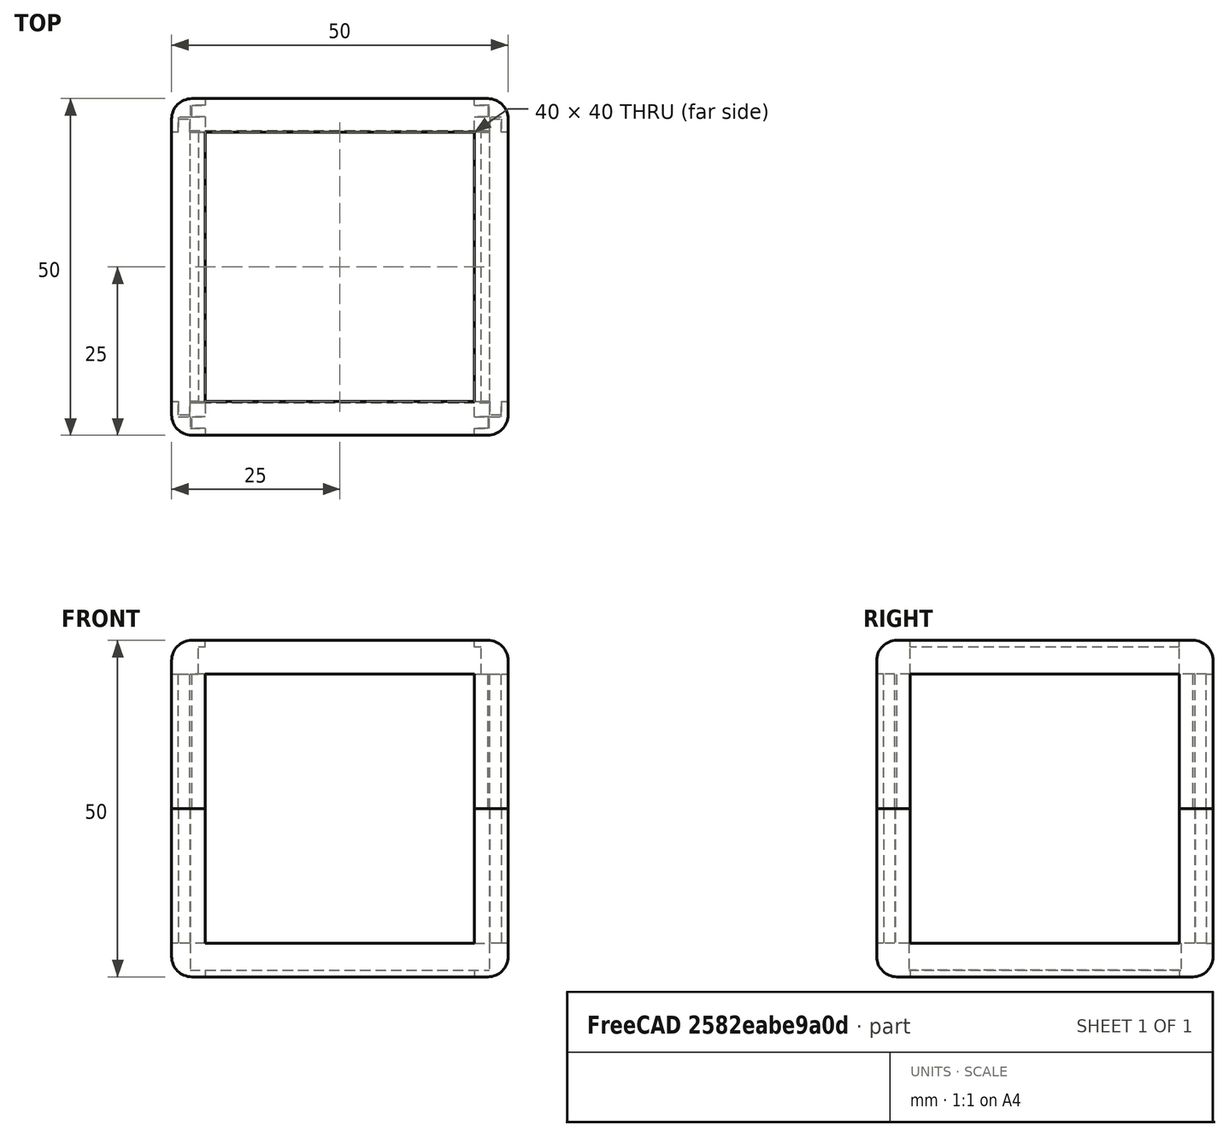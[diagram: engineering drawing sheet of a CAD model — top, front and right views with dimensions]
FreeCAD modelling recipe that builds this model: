
FCSTD DOCUMENT  (FreeCAD 0.18.4R)
Label: frame
License: All rights reserved
LicenseURL: http://en.wikipedia.org/wiki/All_rights_reserved
objects: Sketcher::SketchObject×8, PartDesign::Pocket×6, PartDesign::Pad×2, PartDesign::Fillet×2, PartDesign::Body×2, Mesh::Feature×1
note: 28 computed .brp shape members not serialized (recipe doc carries the construction recipe); baked Part::Feature solids carry a one-line shape summary decoded from their .brp

FEATURE [Sketcher::SketchObject] Sketch
  MapMode = 5
  Support = -> [XY_Plane]
  sketch-geometry (4):
    g0: LineSegment StartX=-25 StartY=25 StartZ=0 EndX=25 EndY=25 EndZ=0
    g1: LineSegment StartX=25 StartY=25 StartZ=0 EndX=25 EndY=-25 EndZ=0
    g2: LineSegment StartX=25 StartY=-25 StartZ=0 EndX=-25 EndY=-25 EndZ=0
    g3: LineSegment StartX=-25 StartY=-25 StartZ=0 EndX=-25 EndY=25 EndZ=0
  constraints (10):
    c: Coincident(g0,g1)
    c: Coincident(g1,g2)
    c: Coincident(g2,g3)
    c: Coincident(g3,g0)
    c: Horizontal(g0)
    c: Vertical(g3)
    c: DistanceX(g0,g0) = 50
    c: DistanceY(g1,g1) = 50
    c: Symmetric(g2,g1,g-2)
    c: Symmetric(g0,g1,g-1)
FEATURE [PartDesign::Pad] Pad
  Length = 25
  Length2 = 100
  Profile = -> Sketch
  Type = 0
FEATURE [PartDesign::Fillet] Fillet
  Base = -> Pad [Edge9,Edge11,Edge3,Edge6,Edge8,Edge2,Edge1,Edge5]
  BaseFeature = -> Pad
  Radius = 3
FEATURE [Sketcher::SketchObject] Sketch007
  MapMode = 5
  Placement = pos=(0,0,25) rot=(0,0,1;0rad)
  Support = -> [Fillet]
  sketch-geometry (44):
    g0: LineSegment StartX=-20 StartY=25 StartZ=0 EndX=-20 EndY=24 EndZ=0
    g1: LineSegment StartX=-20 StartY=24 StartZ=0 EndX=-22.25 EndY=24 EndZ=0
    g2: LineSegment StartX=-22.25 StartY=24 StartZ=0 EndX=-22.25 EndY=22.3 EndZ=0
    g3: LineSegment StartX=-22.25 StartY=22.3 StartZ=0 EndX=-20 EndY=22.3 EndZ=0
    g4: LineSegment StartX=-20 StartY=22.3 StartZ=0 EndX=-20 EndY=20 EndZ=0
    g5: LineSegment StartX=-20 StartY=20 StartZ=0 EndX=-22.3 EndY=20 EndZ=0
    g6: LineSegment StartX=-22.3 StartY=20 StartZ=0 EndX=-22.3 EndY=22.25 EndZ=0
    g7: LineSegment StartX=-22.3 StartY=22.25 StartZ=0 EndX=-24 EndY=22.25 EndZ=0
    g8: LineSegment StartX=-24 StartY=22.25 StartZ=0 EndX=-24 EndY=20 EndZ=0
    g9: LineSegment StartX=-24 StartY=20 StartZ=0 EndX=-25 EndY=20 EndZ=0
    g10: LineSegment StartX=-25 StartY=20 StartZ=0 EndX=-25 EndY=-20 EndZ=0
    g11: LineSegment StartX=-25 StartY=-20 StartZ=0 EndX=-24 EndY=-20 EndZ=0
    g12: LineSegment StartX=-24 StartY=-20 StartZ=0 EndX=-24 EndY=-22.25 EndZ=0
    g13: LineSegment StartX=-24 StartY=-22.25 StartZ=0 EndX=-22.3 EndY=-22.25 EndZ=0
    g14: LineSegment StartX=-22.3 StartY=-22.25 StartZ=0 EndX=-22.3 EndY=-20 EndZ=0
    g15: LineSegment StartX=-22.3 StartY=-20 StartZ=0 EndX=-20 EndY=-20 EndZ=0
    g16: LineSegment StartX=-20 StartY=-20 StartZ=0 EndX=-20 EndY=-22.3 EndZ=0
    g17: LineSegment StartX=-20 StartY=-22.3 StartZ=0 EndX=-22.25 EndY=-22.3 EndZ=0
    g18: LineSegment StartX=-22.25 StartY=-22.3 StartZ=0 EndX=-22.25 EndY=-24 EndZ=0
    g19: LineSegment StartX=-22.25 StartY=-24 StartZ=0 EndX=-20 EndY=-24 EndZ=0
    g20: LineSegment StartX=-20 StartY=-24 StartZ=0 EndX=-20 EndY=-25 EndZ=0
    g21: LineSegment StartX=-20 StartY=-25 StartZ=0 EndX=20 EndY=-25 EndZ=0
    g22: LineSegment StartX=20 StartY=-25 StartZ=0 EndX=20 EndY=-24 EndZ=0
    g23: LineSegment StartX=20 StartY=-24 StartZ=0 EndX=22.25 EndY=-24 EndZ=0
    g24: LineSegment StartX=22.25 StartY=-24 StartZ=0 EndX=22.25 EndY=-22.3 EndZ=0
    g25: LineSegment StartX=22.25 StartY=-22.3 StartZ=0 EndX=20 EndY=-22.3 EndZ=0
    g26: LineSegment StartX=20 StartY=-22.3 StartZ=0 EndX=20 EndY=-20 EndZ=0
    g27: LineSegment StartX=20 StartY=-20 StartZ=0 EndX=22.3 EndY=-20 EndZ=0
    g28: LineSegment StartX=22.3 StartY=-20 StartZ=0 EndX=22.3 EndY=-22.25 EndZ=0
    g29: LineSegment StartX=22.3 StartY=-22.25 StartZ=0 EndX=24 EndY=-22.25 EndZ=0
    g30: LineSegment StartX=24 StartY=-22.25 StartZ=0 EndX=24 EndY=-20 EndZ=0
    g31: LineSegment StartX=24 StartY=-20 StartZ=0 EndX=25 EndY=-20 EndZ=0
    g32: LineSegment StartX=25 StartY=-20 StartZ=0 EndX=25 EndY=20 EndZ=0
    g33: LineSegment StartX=25 StartY=20 StartZ=0 EndX=24 EndY=20 EndZ=0
    g34: LineSegment StartX=24 StartY=20 StartZ=0 EndX=24 EndY=22.25 EndZ=0
    g35: LineSegment StartX=24 StartY=22.25 StartZ=0 EndX=22.3 EndY=22.25 EndZ=0
    g36: LineSegment StartX=22.3 StartY=22.25 StartZ=0 EndX=22.3 EndY=20 EndZ=0
    g37: LineSegment StartX=22.3 StartY=20 StartZ=0 EndX=20 EndY=20 EndZ=0
    g38: LineSegment StartX=20 StartY=20 StartZ=0 EndX=20 EndY=22.3 EndZ=0
    g39: LineSegment StartX=20 StartY=22.3 StartZ=0 EndX=22.25 EndY=22.3 EndZ=0
    g40: LineSegment StartX=22.25 StartY=22.3 StartZ=0 EndX=22.25 EndY=24 EndZ=0
    g41: LineSegment StartX=22.25 StartY=24 StartZ=0 EndX=20 EndY=24 EndZ=0
    g42: LineSegment StartX=20 StartY=24 StartZ=0 EndX=20 EndY=25 EndZ=0
    g43: LineSegment StartX=20 StartY=25 StartZ=0 EndX=-20 EndY=25 EndZ=0
  constraints (130):
    c: Coincident(g0,g1)
    c: Coincident(g1,g2)
    c: Coincident(g2,g3)
    c: Coincident(g3,g4)
    c: Coincident(g4,g5)
    c: Horizontal(g5)
    c: Coincident(g5,g6)
    c: Vertical(g6)
    c: Coincident(g6,g7)
    c: Horizontal(g7)
    c: Coincident(g7,g8)
    c: Vertical(g8)
    c: Coincident(g8,g9)
    c: Coincident(g9,g10)
    c: Vertical(g10)
    c: Coincident(g10,g11)
    c: Coincident(g11,g12)
    c: Coincident(g12,g13)
    c: Coincident(g13,g14)
    c: Vertical(g14)
    c: Coincident(g14,g15)
    c: Horizontal(g15)
    c: Coincident(g15,g16)
    c: Coincident(g16,g17)
    c: Horizontal(g17)
    c: Coincident(g17,g18)
    c: Coincident(g18,g19)
    c: Coincident(g19,g20)
    c: Coincident(g20,g21)
    c: Horizontal(g21)
    c: Coincident(g21,g22)
    c: Coincident(g22,g23)
    c: Horizontal(g23)
    c: Coincident(g23,g24)
    c: Coincident(g24,g25)
    c: Horizontal(g25)
    c: Coincident(g25,g26)
    c: Vertical(g26)
    c: Coincident(g26,g27)
    c: Coincident(g27,g28)
    c: Coincident(g28,g29)
    c: Coincident(g29,g30)
    c: Vertical(g30)
    c: Coincident(g30,g31)
    c: Horizontal(g31)
    c: Coincident(g31,g32)
    c: Vertical(g32)
    c: Coincident(g32,g33)
    c: Coincident(g33,g34)
    c: Vertical(g34)
    c: Coincident(g34,g35)
    c: Coincident(g35,g36)
    c: Coincident(g36,g37)
    c: Coincident(g37,g38)
    c: Coincident(g38,g39)
    c: Coincident(g39,g40)
    c: Coincident(g40,g41)
    c: Coincident(g41,g42)
    c: Vertical(g42)
    c: Coincident(g42,g43)
    c: Coincident(g43,g0)
    c: Equal(g43,g21)
    c: Horizontal(g43)
    c: Equal(g10,g32)
    c: Horizontal(g13)
    c: Horizontal(g11)
    c: Vertical(g16)
    c: Vertical(g12)
    c: Vertical(g18)
    c: Vertical(g20)
    c: Horizontal(g19)
    c: Vertical(g22)
    c: Vertical(g24)
    c: Vertical(g28)
    c: Vertical(g36)
    c: Vertical(g38)
    c: Vertical(g2)
    c: Vertical(g0)
    c: Horizontal(g1)
    c: Horizontal(g3)
    c: Horizontal(g9)
    c: Horizontal(g27)
    c: Horizontal(g33)
    c: Horizontal(g35)
    c: Horizontal(g37)
    c: Horizontal(g39)
    c: Equal(g2,g40)
    c: Equal(g40,g18)
    c: Equal(g18,g24)
    c: Equal(g13,g29)
    c: Equal(g29,g35)
    c: Equal(g35,g7)
    c: Equal(g33,g9)
    c: Equal(g9,g11)
    c: Equal(g11,g31)
    c: Equal(g22,g20)
    c: Equal(g20,g0)
    c: Equal(g0,g42)
    c: Equal(g4,g38)
    c: Equal(g38,g26)
    c: Equal(g26,g16)
    c: Equal(g15,g27)
    c: Equal(g27,g37)
    c: Equal(g37,g5)
    c: Equal(g8,g6)
    c: Equal(g6,g36)
    c: Equal(g36,g34)
    c: Equal(g34,g12)
    c: Equal(g12,g14)
    c: Equal(g14,g28)
    c: Equal(g28,g30)
    c: Equal(g25,g23)
    c: Equal(g23,g17)
    c: Equal(g17,g19)
    c: Equal(g19,g1)
    c: Equal(g1,g3)
    c: Equal(g3,g41)
    c: Equal(g41,g39)
    c: DistanceX(g43,g43) = 40
    c: DistanceY(g32,g32) = 40
    c: DistanceY(g12,g7) = 44.5
    c: DistanceX(g1,g40) = 44.5
    c: DistanceY(g20,g0) = 50
    c: DistanceX(g10,g31) = 50
    c: Symmetric(g21,g42,g-1)
    c: Symmetric(g9,g32,g-2)
    c: DistanceX(g13,g13) = 1.7
    c: DistanceX(g11,g11) = 1
    c: DistanceY(g20,g20) = 1
    c: DistanceY(g18,g18) = 1.7
FEATURE [PartDesign::Pocket] Pocket
  BaseFeature = -> Fillet
  Length = 20
  Length2 = 100
  Profile = -> Sketch007
  Type = 0
FEATURE [Mesh::Feature] screen
  Placement = pos=(-18,10,5.5) rot=(-1,0,0;3.14159rad)
FEATURE [Sketcher::SketchObject] Sketch008
  MapMode = 5
  Placement = pos=(0,0,5) rot=(0,0,1;0rad)
  Support = -> [Pocket]
  sketch-geometry (4):
    g0: LineSegment StartX=-22.25 StartY=20.25 StartZ=0 EndX=22.25 EndY=20.25 EndZ=0
    g1: LineSegment StartX=22.25 StartY=20.25 StartZ=0 EndX=22.25 EndY=-20.25 EndZ=0
    g2: LineSegment StartX=22.25 StartY=-20.25 StartZ=0 EndX=-22.25 EndY=-20.25 EndZ=0
    g3: LineSegment StartX=-22.25 StartY=-20.25 StartZ=0 EndX=-22.25 EndY=20.25 EndZ=0
  constraints (10):
    c: Coincident(g0,g1)
    c: Coincident(g1,g2)
    c: Coincident(g2,g3)
    c: Coincident(g3,g0)
    c: Horizontal(g0)
    c: Vertical(g3)
    c: DistanceX(g0,g0) = 44.5
    c: DistanceY(g1,g1) = 40.5
    c: Symmetric(g2,g1,g-2)
    c: Symmetric(g0,g1,g-1)
FEATURE [PartDesign::Pocket] Pocket001
  BaseFeature = -> Pocket
  Length = 4
  Length2 = 100
  Profile = -> Sketch008
  Type = 0
FEATURE [Sketcher::SketchObject] Sketch009
  MapMode = 5
  Placement = pos=(0,0,1) rot=(0,0,1;0rad)
  Support = -> [Pocket001]
  sketch-geometry (4):
    g0: LineSegment StartX=-20 StartY=20 StartZ=0 EndX=20 EndY=20 EndZ=0
    g1: LineSegment StartX=20 StartY=20 StartZ=0 EndX=20 EndY=-20 EndZ=0
    g2: LineSegment StartX=20 StartY=-20 StartZ=0 EndX=-20 EndY=-20 EndZ=0
    g3: LineSegment StartX=-20 StartY=-20 StartZ=0 EndX=-20 EndY=20 EndZ=0
  constraints (10):
    c: Coincident(g0,g1)
    c: Coincident(g1,g2)
    c: Coincident(g2,g3)
    c: Coincident(g3,g0)
    c: Horizontal(g0)
    c: Vertical(g3)
    c: DistanceY(g1,g1) = 40
    c: DistanceX(g2,g2) = 40
    c: Symmetric(g2,g1,g-2)
    c: Symmetric(g0,g1,g-1)
FEATURE [PartDesign::Pocket] Pocket002
  BaseFeature = -> Pocket001
  Length = 1
  Length2 = 100
  Profile = -> Sketch009
  Type = 0
FEATURE [PartDesign::Body] Body  label="Bottom"
  Group = -> [Sketch,Pad,Fillet,Sketch007,Pocket,Sketch008,Pocket001,Sketch009,Pocket002]
  Origin = -> Origin
  Tip = -> Pocket002
FEATURE [Sketcher::SketchObject] Sketch011
  MapMode = 5
  Support = -> [XY_Plane001]
  sketch-geometry (4):
    g0: LineSegment StartX=-25 StartY=25 StartZ=0 EndX=25 EndY=25 EndZ=0
    g1: LineSegment StartX=25 StartY=25 StartZ=0 EndX=25 EndY=-25 EndZ=0
    g2: LineSegment StartX=25 StartY=-25 StartZ=0 EndX=-25 EndY=-25 EndZ=0
    g3: LineSegment StartX=-25 StartY=-25 StartZ=0 EndX=-25 EndY=25 EndZ=0
  constraints (10):
    c: Coincident(g0,g1)
    c: Coincident(g1,g2)
    c: Coincident(g2,g3)
    c: Coincident(g3,g0)
    c: Horizontal(g0)
    c: Vertical(g3)
    c: DistanceX(g0,g0) = 50
    c: DistanceY(g1,g1) = 50
    c: Symmetric(g2,g1,g-2)
    c: Symmetric(g0,g1,g-1)
FEATURE [PartDesign::Pad] Pad001
  Length = 25
  Length2 = 100
  Profile = -> Sketch011
  Type = 0
FEATURE [PartDesign::Fillet] Fillet001
  Base = -> Pad001 [Edge9,Edge11,Edge3,Edge6,Edge8,Edge2,Edge1,Edge5]
  BaseFeature = -> Pad001
  Radius = 3
FEATURE [Sketcher::SketchObject] Sketch012
  MapMode = 5
  Placement = pos=(0,0,25) rot=(0,0,1;0rad)
  Support = -> [Fillet001]
  sketch-geometry (44):
    g0: LineSegment StartX=-20 StartY=25 StartZ=0 EndX=-20 EndY=24 EndZ=0
    g1: LineSegment StartX=-20 StartY=24 StartZ=0 EndX=-22 EndY=24 EndZ=0
    g2: LineSegment StartX=-22 StartY=24 StartZ=0 EndX=-22 EndY=22.3 EndZ=0
    g3: LineSegment StartX=-22 StartY=22.3 StartZ=0 EndX=-20 EndY=22.3 EndZ=0
    g4: LineSegment StartX=-20 StartY=22.3 StartZ=0 EndX=-20 EndY=20 EndZ=0
    g5: LineSegment StartX=-20 StartY=20 StartZ=0 EndX=-22.3 EndY=20 EndZ=0
    g6: LineSegment StartX=-22.3 StartY=20 StartZ=0 EndX=-22.3 EndY=22 EndZ=0
    g7: LineSegment StartX=-22.3 StartY=22 StartZ=0 EndX=-24 EndY=22 EndZ=0
    g8: LineSegment StartX=-24 StartY=22 StartZ=0 EndX=-24 EndY=20 EndZ=0
    g9: LineSegment StartX=-24 StartY=20 StartZ=0 EndX=-25 EndY=20 EndZ=0
    g10: LineSegment StartX=-25 StartY=20 StartZ=0 EndX=-25 EndY=-20 EndZ=0
    g11: LineSegment StartX=-25 StartY=-20 StartZ=0 EndX=-24 EndY=-20 EndZ=0
    g12: LineSegment StartX=-24 StartY=-20 StartZ=0 EndX=-24 EndY=-22 EndZ=0
    g13: LineSegment StartX=-24 StartY=-22 StartZ=0 EndX=-22.3 EndY=-22 EndZ=0
    g14: LineSegment StartX=-22.3 StartY=-22 StartZ=0 EndX=-22.3 EndY=-20 EndZ=0
    g15: LineSegment StartX=-22.3 StartY=-20 StartZ=0 EndX=-20 EndY=-20 EndZ=0
    g16: LineSegment StartX=-20 StartY=-20 StartZ=0 EndX=-20 EndY=-22.3 EndZ=0
    g17: LineSegment StartX=-20 StartY=-22.3 StartZ=0 EndX=-22 EndY=-22.3 EndZ=0
    g18: LineSegment StartX=-22 StartY=-22.3 StartZ=0 EndX=-22 EndY=-24 EndZ=0
    g19: LineSegment StartX=-22 StartY=-24 StartZ=0 EndX=-20 EndY=-24 EndZ=0
    g20: LineSegment StartX=-20 StartY=-24 StartZ=0 EndX=-20 EndY=-25 EndZ=0
    g21: LineSegment StartX=-20 StartY=-25 StartZ=0 EndX=20 EndY=-25 EndZ=0
    g22: LineSegment StartX=20 StartY=-25 StartZ=0 EndX=20 EndY=-24 EndZ=0
    g23: LineSegment StartX=20 StartY=-24 StartZ=0 EndX=22 EndY=-24 EndZ=0
    g24: LineSegment StartX=22 StartY=-24 StartZ=0 EndX=22 EndY=-22.3 EndZ=0
    g25: LineSegment StartX=22 StartY=-22.3 StartZ=0 EndX=20 EndY=-22.3 EndZ=0
    g26: LineSegment StartX=20 StartY=-22.3 StartZ=0 EndX=20 EndY=-20 EndZ=0
    g27: LineSegment StartX=20 StartY=-20 StartZ=0 EndX=22.3 EndY=-20 EndZ=0
    g28: LineSegment StartX=22.3 StartY=-20 StartZ=0 EndX=22.3 EndY=-22 EndZ=0
    g29: LineSegment StartX=22.3 StartY=-22 StartZ=0 EndX=24 EndY=-22 EndZ=0
    g30: LineSegment StartX=24 StartY=-22 StartZ=0 EndX=24 EndY=-20 EndZ=0
    g31: LineSegment StartX=24 StartY=-20 StartZ=0 EndX=25 EndY=-20 EndZ=0
    g32: LineSegment StartX=25 StartY=-20 StartZ=0 EndX=25 EndY=20 EndZ=0
    g33: LineSegment StartX=25 StartY=20 StartZ=0 EndX=24 EndY=20 EndZ=0
    g34: LineSegment StartX=24 StartY=20 StartZ=0 EndX=24 EndY=22 EndZ=0
    g35: LineSegment StartX=24 StartY=22 StartZ=0 EndX=22.3 EndY=22 EndZ=0
    g36: LineSegment StartX=22.3 StartY=22 StartZ=0 EndX=22.3 EndY=20 EndZ=0
    g37: LineSegment StartX=22.3 StartY=20 StartZ=0 EndX=20 EndY=20 EndZ=0
    g38: LineSegment StartX=20 StartY=20 StartZ=0 EndX=20 EndY=22.3 EndZ=0
    g39: LineSegment StartX=20 StartY=22.3 StartZ=0 EndX=22 EndY=22.3 EndZ=0
    g40: LineSegment StartX=22 StartY=22.3 StartZ=0 EndX=22 EndY=24 EndZ=0
    g41: LineSegment StartX=22 StartY=24 StartZ=0 EndX=20 EndY=24 EndZ=0
    g42: LineSegment StartX=20 StartY=24 StartZ=0 EndX=20 EndY=25 EndZ=0
    g43: LineSegment StartX=20 StartY=25 StartZ=0 EndX=-20 EndY=25 EndZ=0
  constraints (130):
    c: Coincident(g0,g1)
    c: Coincident(g1,g2)
    c: Coincident(g2,g3)
    c: Coincident(g3,g4)
    c: Coincident(g4,g5)
    c: Horizontal(g5)
    c: Coincident(g5,g6)
    c: Vertical(g6)
    c: Coincident(g6,g7)
    c: Horizontal(g7)
    c: Coincident(g7,g8)
    c: Vertical(g8)
    c: Coincident(g8,g9)
    c: Coincident(g9,g10)
    c: Vertical(g10)
    c: Coincident(g10,g11)
    c: Coincident(g11,g12)
    c: Coincident(g12,g13)
    c: Coincident(g13,g14)
    c: Vertical(g14)
    c: Coincident(g14,g15)
    c: Horizontal(g15)
    c: Coincident(g15,g16)
    c: Coincident(g16,g17)
    c: Horizontal(g17)
    c: Coincident(g17,g18)
    c: Coincident(g18,g19)
    c: Coincident(g19,g20)
    c: Coincident(g20,g21)
    c: Horizontal(g21)
    c: Coincident(g21,g22)
    c: Coincident(g22,g23)
    c: Horizontal(g23)
    c: Coincident(g23,g24)
    c: Coincident(g24,g25)
    c: Horizontal(g25)
    c: Coincident(g25,g26)
    c: Vertical(g26)
    c: Coincident(g26,g27)
    c: Coincident(g27,g28)
    c: Coincident(g28,g29)
    c: Coincident(g29,g30)
    c: Vertical(g30)
    c: Coincident(g30,g31)
    c: Horizontal(g31)
    c: Coincident(g31,g32)
    c: Vertical(g32)
    c: Coincident(g32,g33)
    c: Coincident(g33,g34)
    c: Vertical(g34)
    c: Coincident(g34,g35)
    c: Coincident(g35,g36)
    c: Coincident(g36,g37)
    c: Coincident(g37,g38)
    c: Coincident(g38,g39)
    c: Coincident(g39,g40)
    c: Coincident(g40,g41)
    c: Coincident(g41,g42)
    c: Vertical(g42)
    c: Coincident(g42,g43)
    c: Coincident(g43,g0)
    c: Equal(g43,g21)
    c: Horizontal(g43)
    c: Equal(g10,g32)
    c: Horizontal(g13)
    c: Horizontal(g11)
    c: Vertical(g16)
    c: Vertical(g12)
    c: Vertical(g18)
    c: Vertical(g20)
    c: Horizontal(g19)
    c: Vertical(g22)
    c: Vertical(g24)
    c: Vertical(g28)
    c: Vertical(g36)
    c: Vertical(g38)
    c: Vertical(g2)
    c: Vertical(g0)
    c: Horizontal(g1)
    c: Horizontal(g3)
    c: Horizontal(g9)
    c: Horizontal(g27)
    c: Horizontal(g33)
    c: Horizontal(g35)
    c: Horizontal(g37)
    c: Horizontal(g39)
    c: Equal(g2,g40)
    c: Equal(g40,g18)
    c: Equal(g18,g24)
    c: Equal(g13,g29)
    c: Equal(g29,g35)
    c: Equal(g35,g7)
    c: Equal(g33,g9)
    c: Equal(g9,g11)
    c: Equal(g11,g31)
    c: Equal(g22,g20)
    c: Equal(g20,g0)
    c: Equal(g0,g42)
    c: Equal(g4,g38)
    c: Equal(g38,g26)
    c: Equal(g26,g16)
    c: Equal(g15,g27)
    c: Equal(g27,g37)
    c: Equal(g37,g5)
    c: Equal(g8,g6)
    c: Equal(g6,g36)
    c: Equal(g36,g34)
    c: Equal(g34,g12)
    c: Equal(g12,g14)
    c: Equal(g14,g28)
    c: Equal(g28,g30)
    c: Equal(g25,g23)
    c: Equal(g23,g17)
    c: Equal(g17,g19)
    c: Equal(g19,g1)
    c: Equal(g1,g3)
    c: Equal(g3,g41)
    c: Equal(g41,g39)
    c: DistanceX(g43,g43) = 40
    c: DistanceY(g32,g32) = 40
    c: DistanceY(g12,g7) = 44
    c: DistanceX(g1,g40) = 44
    c: DistanceY(g20,g0) = 50
    c: DistanceX(g10,g31) = 50
    c: Symmetric(g21,g42,g-1)
    c: Symmetric(g9,g32,g-2)
    c: DistanceX(g13,g13) = 1.7
    c: DistanceX(g11,g11) = 1
    c: DistanceY(g20,g20) = 1
    c: DistanceY(g18,g18) = 1.7
FEATURE [PartDesign::Pocket] Pocket004
  BaseFeature = -> Fillet001
  Length = 20
  Length2 = 100
  Profile = -> Sketch012
  Type = 0
FEATURE [Sketcher::SketchObject] Sketch013
  MapMode = 5
  Placement = pos=(0,0,5) rot=(0,0,1;0rad)
  Support = -> [Pocket004]
  sketch-geometry (4):
    g0: LineSegment StartX=-21 StartY=20 StartZ=0 EndX=21 EndY=20 EndZ=0
    g1: LineSegment StartX=21 StartY=20 StartZ=0 EndX=21 EndY=-20 EndZ=0
    g2: LineSegment StartX=21 StartY=-20 StartZ=0 EndX=-21 EndY=-20 EndZ=0
    g3: LineSegment StartX=-21 StartY=-20 StartZ=0 EndX=-21 EndY=20 EndZ=0
  constraints (10):
    c: Coincident(g0,g1)
    c: Coincident(g1,g2)
    c: Coincident(g2,g3)
    c: Coincident(g3,g0)
    c: Horizontal(g0)
    c: Vertical(g3)
    c: DistanceX(g0,g0) = 42
    c: DistanceY(g1,g1) = 40
    c: Symmetric(g2,g1,g-2)
    c: Symmetric(g0,g1,g-1)
FEATURE [PartDesign::Pocket] Pocket003
  BaseFeature = -> Pocket004
  Length = 4
  Length2 = 100
  Profile = -> Sketch013
  Type = 0
FEATURE [Sketcher::SketchObject] Sketch010
  MapMode = 5
  Placement = pos=(0,0,1) rot=(0,0,1;0rad)
  Support = -> [Pocket003]
  sketch-geometry (4):
    g0: LineSegment StartX=-20 StartY=20 StartZ=0 EndX=20 EndY=20 EndZ=0
    g1: LineSegment StartX=20 StartY=20 StartZ=0 EndX=20 EndY=-20 EndZ=0
    g2: LineSegment StartX=20 StartY=-20 StartZ=0 EndX=-20 EndY=-20 EndZ=0
    g3: LineSegment StartX=-20 StartY=-20 StartZ=0 EndX=-20 EndY=20 EndZ=0
  constraints (10):
    c: Coincident(g0,g1)
    c: Coincident(g1,g2)
    c: Coincident(g2,g3)
    c: Coincident(g3,g0)
    c: Horizontal(g0)
    c: Vertical(g3)
    c: DistanceY(g1,g1) = 40
    c: DistanceX(g2,g2) = 40
    c: Symmetric(g2,g1,g-2)
    c: Symmetric(g0,g1,g-1)
FEATURE [PartDesign::Pocket] Pocket005
  BaseFeature = -> Pocket003
  Length = 1
  Length2 = 100
  Profile = -> Sketch010
  Type = 0
FEATURE [PartDesign::Body] Body001  label="top"
  Group = -> [Sketch011,Pad001,Fillet001,Sketch012,Pocket004,Sketch013,Pocket003,Sketch010,Pocket005]
  Origin = -> Origin001
  Placement = pos=(0,0,50) rot=(0,1,0;3.14159rad)
  Tip = -> Pocket005
